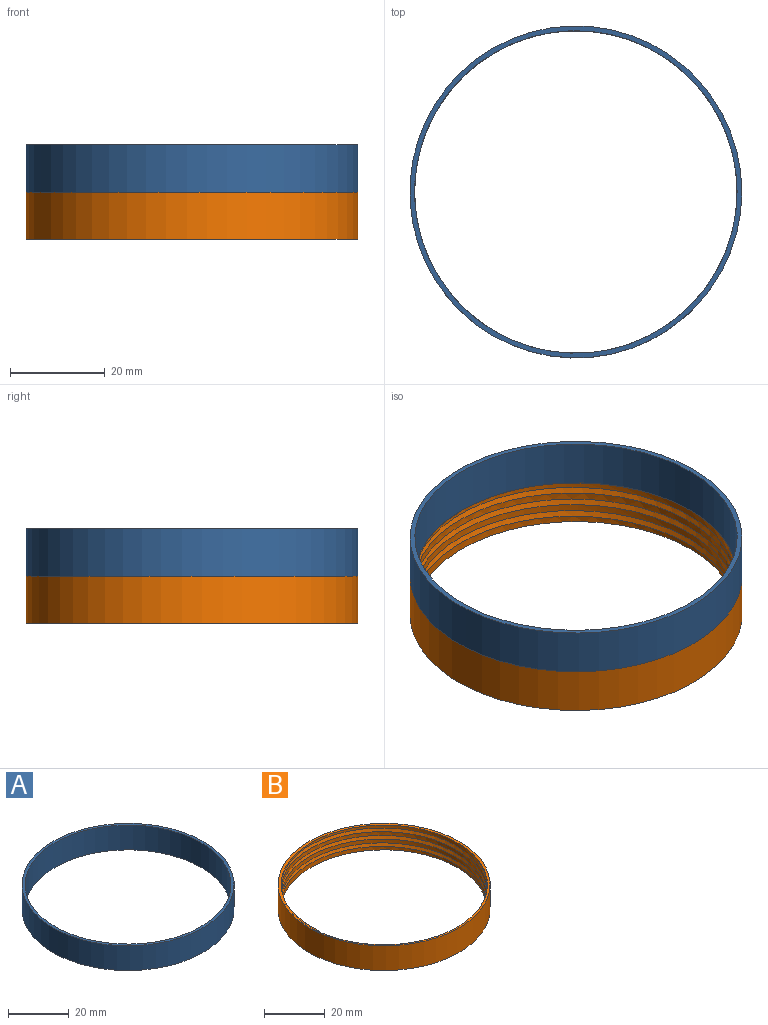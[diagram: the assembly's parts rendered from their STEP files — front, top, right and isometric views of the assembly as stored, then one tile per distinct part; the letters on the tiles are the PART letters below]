
ASSEMBLY  parts=2 mates=1
PART A: 4 faces, bbox 70x70x10 mm
  f0: cylinder r=35mm len=70mm, axis (0,0,-1), area 2199.1mm2, adj f1,f2
  f1: plane 70x70mm, normal (0,0,1), area 216.8mm2, adj f0,f3
  f2: plane 70x70mm, normal (0,0,-1), area 216.8mm2, adj f0,f3
  f3: cylinder r=34mm len=68mm, axis (0,0,-1), area 2136.3mm2, adj f1,f2
PART B: 7 faces, bbox 70.8x80.5x12.2 mm
  f0: cylinder r=35mm len=70mm, axis (0,0,-1), area 2199.1mm2, adj f1,f2
  f1: plane 70.79x70.79mm, normal (0,0,1), area 190.7mm2, adj f0,f3,f5,f6
  f2: plane 70x70mm, normal (0,0,-1), area 216.8mm2, adj f0,f3
  f3: cylinder r=34mm len=68mm, axis (0,0,-1), area 1180.1mm2, adj f1,f2,f4,f5,f6
  f4: plane 1.45x0.43mm, normal (0.87,-0.5,0), area 0.4mm2, adj f3,f5,f6
  f5: bspline ~79.67x69mm, area 306.7mm2, adj f1,f3,f4,f6
  f6: bspline ~79.67x69mm, area 1020.3mm2, adj f1,f3,f4,f5
PLACE A t=(-2.45,-11.79,25.96)mm
PLACE B t=(-2.45,-11.79,15.96)mm
MATE fastened A.f3 <-> B.f0  axis (0,0,-1) through (-2.45,-11.79,25.96)mm
